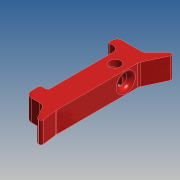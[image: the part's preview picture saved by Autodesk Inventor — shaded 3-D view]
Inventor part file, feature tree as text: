
AUTODESK INVENTOR PART (.ipt)
format: ipt  version: 2015 SP1 (Build 190203100, 203)  size: 314,368 bytes
history: native  units: mm
features: fillet x10, hole x2, sketch x2, extrude x1
ambient origin geometry x8: Origin, YZ Plane, XZ Plane, XY Plane, X Axis, Y Axis, Z Axis, Center Point
bodies: Solid1 (feature_tree)
feature tree (15):
  extrude  "Extrusion1"  Depth=14.0mm
  fillet  "Fillet1"  Radius=20.0mm
  fillet  "Fillet2"  Radius=22.0mm
  fillet  "Fillet3"  Radius=30.0mm
  fillet  "Fillet4"  Radius=4.1mm
  fillet  "Fillet5"  Radius=3.0mm
  hole  "Hole1"  [1 undecoded]
  fillet  "Fillet6"  Radius=9.0mm
  fillet  "Fillet8"  [1 undecoded]
  fillet  "Fillet9"  Radius=16.0mm
  fillet  "Fillet10"  Radius=7.0mm
  fillet  "Fillet11"  Radius=3.5mm
  hole  "Hole2"  [1 undecoded]
  sketch  "Sketch2"  dims[d1=3.0mm d2=5.0mm d3=14.0mm d4=20.0mm d5=22.0mm d6=30.0mm d7=4.1mm d8=3.0mm]
  sketch  "Sketch3"  dims[d9=25.0mm d10=6.0mm d11=9.0mm d12=0.0mm d13=16.0mm d14=7.0mm d15=3.5mm d16=120.0deg d17=1.308997mm d19=5.0mm d20=5.0mm d21=1.0mm d22=1.0mm d23=1.0mm d24=9.8mm d25=0.0mm d26=0.5mm d27=1.0mm d28=3.0mm d29=2.0mm d30=1.0mm d32=5.0mm d33=6.0mm d34=4.0mm d35=2.0mm d36=90.0deg d37=8.0mm d38=20.594885mm d39=2.0mm d40=45.0deg d41=3.0mm d42=10.0mm d43=5.0mm d44=12.0mm d46=1.5mm d47=1.0mm d48=2.0mm d49=1.0mm d50=2.0mm d51=12.0mm d52=5.0mm d53=5.0mm d54=6.0mm d55=4.0mm d56=2.0mm d57=90.0deg d58=8.0mm d59=20.594885mm]
note: 3 required parameter values undecoded (feature->parameter linkage not recoverable at this tier; creation-order binding heuristic only, values carry confidence <= 0.55)
